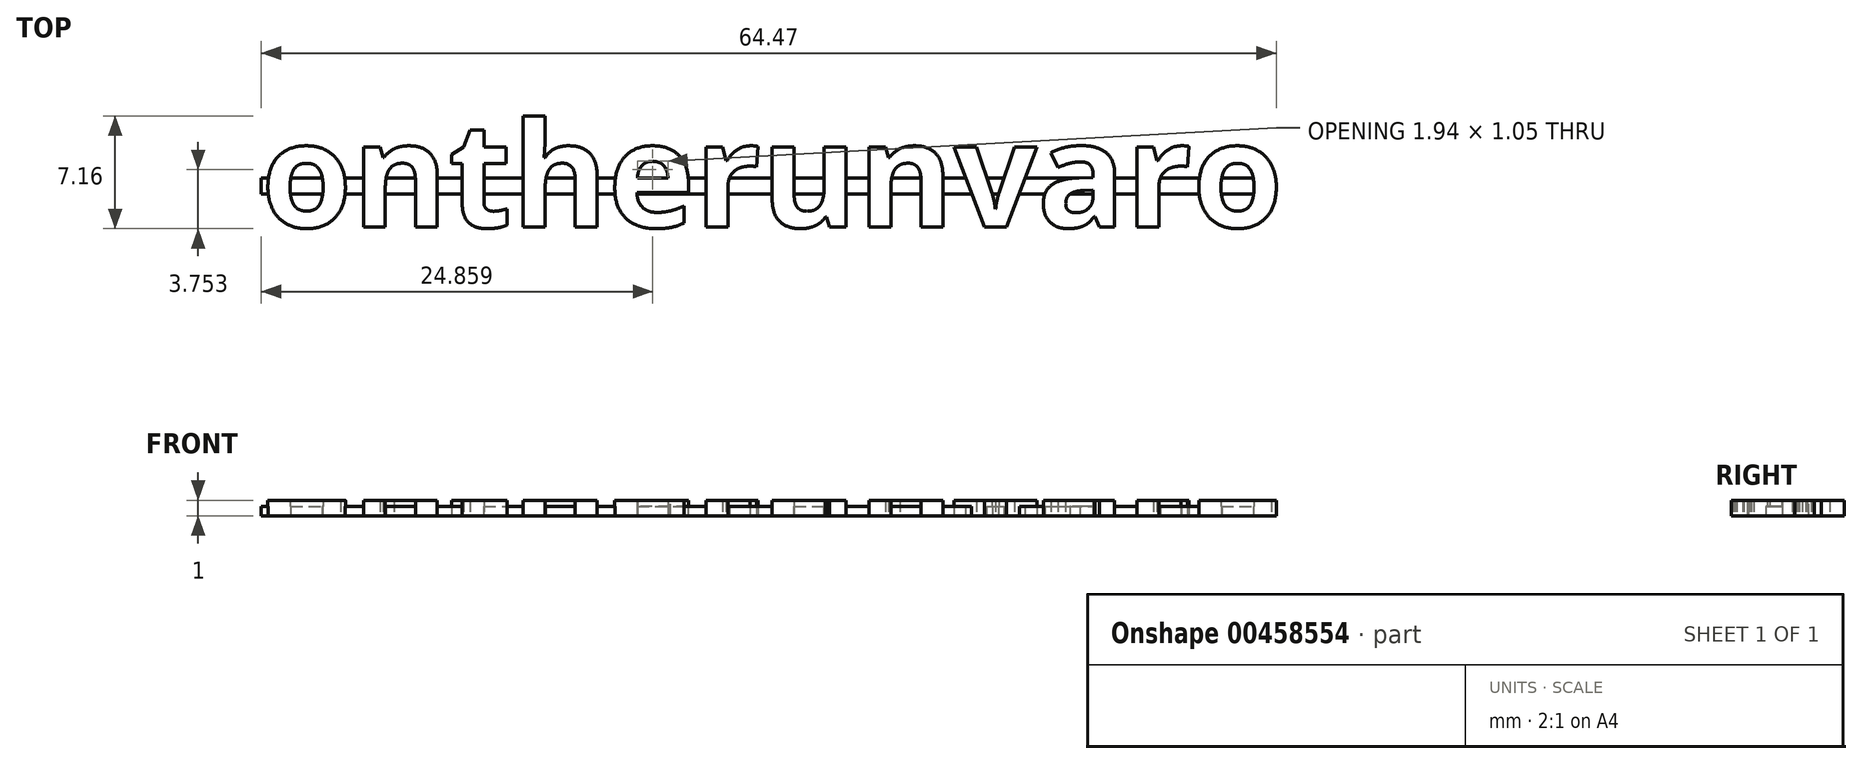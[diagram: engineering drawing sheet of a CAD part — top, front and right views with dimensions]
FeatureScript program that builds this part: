
annotation { "Feature Type Name" : "Feature", "Feature Type Description" : "" }
export const myFeature = defineFeature(function(context is Context, id is Id, definition is map)
    precondition{}
    {
        {
            var Q0;
            Q0=qCreatedBy(makeId("Top.planeOp"),FACE);
            var sketch = newSketch(context, id + "F0", { "sketchPlane" : qUnion([Q0])});
            skText(sketch, "E0", { "text": "ontherunvaro", "fontName": "OpenSans-Bold.ttf"});
            const initialGuessF0  = {"E0": [0, -0.0067, 1, 0, 0.0067]};
            skSetInitialGuess(sketch, initialGuessF0);
            skSolve(sketch);
        }
        {
            var Q0;
            Q0 = qSketchRegion(id + "F0", true);
            extrude(context, id + "F1", {"entities" : qUnion([Q0]), "depth" : 1 * mm});
        }
        {
            var Q0;
            Q0=qCreatedBy(makeId("Top.planeOp"),FACE);
            var sketch = newSketch(context, id + "F2", { "sketchPlane" : qUnion([Q0])});
            skLineSegment(sketch, "E1.bottom", {"start": v(0, -3.56) * mm, "end": v(64.06, -3.56) * mm});
            skLineSegment(sketch, "E1.top", {"start": v(0, -4.6) * mm, "end": v(64.06, -4.6) * mm});
            skLineSegment(sketch, "E1.left", {"start": v(0, -3.56) * mm, "end": v(0, -4.6) * mm});
            skLineSegment(sketch, "E1.right", {"start": v(64.06, -3.56) * mm, "end": v(64.06, -4.6) * mm});
            skSolve(sketch);
        }
        {
            var Q0;
            Q0 = qSketchRegion(id + "F2", true);
            extrude(context, id + "F3", {"entities" : qUnion([Q0]), "operationType" : NewBodyOperationType.ADD, "depth" : 0.6 * mm});
        }
    });
